# Revit family: Albardilla MJ escuadra.C-1
name_source: partatom
category: Modelos genéricos
units: mm (PartAtom-declared; Revit-internal decimal feet)

## family parameters
Compartido = No
Corte con vacíos al cargar = No
Cota de conector redondo = Diámetro de uso
Puede alojar armadura = No
Punto de cálculo de habitación = No
Se basa en plano de trabajo = No
Siempre vertical = No
Tipo de pieza = Normal

## types (10) — shared parameters
Ancho escuadra = 500 mm
Descripción = Pieza de hormigón polímero con anclajes de acero inoxidable
Fabricante = ULMA Architectural Solutions
Material = Hormigón polímero STONEO. Color C-1
URL = https://www.ulmaarchitectural.com
zero-valued in all types: Elevación por defecto

## per-type parameters (varying)
| type | Ancho | Ancho dos | Ancho dos dist. | Ancho total | Anclajes | Dist. primer anclaje +30 | Modelo | Visible dos líneas | Visible una linea |
| MJ12E | 125 mm  [stored 0.410105 ft] | 88 mm | 44 mm | 175 mm  [stored 0.574147 ft] | 88 mm | 138 mm | Albardilla MJ12 en escuadra | No | Sí |
| MJ14E | 150 mm | 100 mm  [stored 0.328084 ft] | 50 mm  [stored 0.164042 ft] | 200 mm  [stored 0.656168 ft] | 100 mm  [stored 0.328084 ft] | 135 mm  [stored 0.442913 ft] | Albardilla MJ14 en escuadra | No | Sí |
| MJ17E | 170 mm  [stored 0.557743 ft] | 110 mm  [stored 0.360892 ft] | 55 mm  [stored 0.180446 ft] | 220 mm  [stored 0.721785 ft] | 110 mm  [stored 0.360892 ft] | 133 mm  [stored 0.436352 ft] | Albardilla MJ17 en escuadra | No | Sí |
| MJ19E | 205 mm  [stored 0.672572 ft] | 128 mm  [stored 0.419948 ft] | 64 mm | 255 mm  [stored 0.836614 ft] | 128 mm  [stored 0.419948 ft] | 130 mm | Albardilla MJ19 en escuadra | No | Sí |
| MJ22E | 220 mm  [stored 0.721785 ft] | 135 mm  [stored 0.442913 ft] | 68 mm | 270 mm  [stored 0.885827 ft] | 135 mm  [stored 0.442913 ft] | 128 mm  [stored 0.419948 ft] | Albardilla MJ22 en escuadra | No | Sí |
| MJ25E | 255 mm  [stored 0.836614 ft] | 153 mm | 76 mm | 305 mm  [stored 1.00066 ft] | 153 mm | 125 mm  [stored 0.410105 ft] | Albardilla MJ25 en escuadra | No | Sí |
| MJ30E | 305 mm  [stored 1.00066 ft] | 178 mm | 89 mm | 355 mm | 178 mm | 120 mm | Albardilla MJ30 en escuadra | Sí | No |
| MJ35E | 350 mm  [stored 1.14829 ft] | 200 mm  [stored 0.656168 ft] | 100 mm  [stored 0.328084 ft] | 400 mm  [stored 1.31234 ft] | 200 mm  [stored 0.656168 ft] | 115 mm  [stored 0.377297 ft] | Albardilla MJ35 en escuadra | Sí | No |
| MJ40E | 400 mm  [stored 1.31234 ft] | 225 mm  [stored 0.738189 ft] | 113 mm | 450 mm  [stored 1.47638 ft] | 225 mm  [stored 0.738189 ft] | 110 mm  [stored 0.360892 ft] | Albardilla MJ40 en escuadra | Sí | No |
| MJ27E | 270 mm  [stored 0.885827 ft] | 160 mm  [stored 0.524934 ft] | 80 mm  [stored 0.262467 ft] | 320 mm  [stored 1.04987 ft] | 160 mm  [stored 0.524934 ft] | 123 mm  [stored 0.403543 ft] | Albardilla MJ27 en escuadra | No | Sí |

note: column(s) folded — value = type name in every type: Código de montaje

note: [stored X ft] marks values corroborated as IEEE doubles in the binary element streams (Revit-internal decimal feet)
